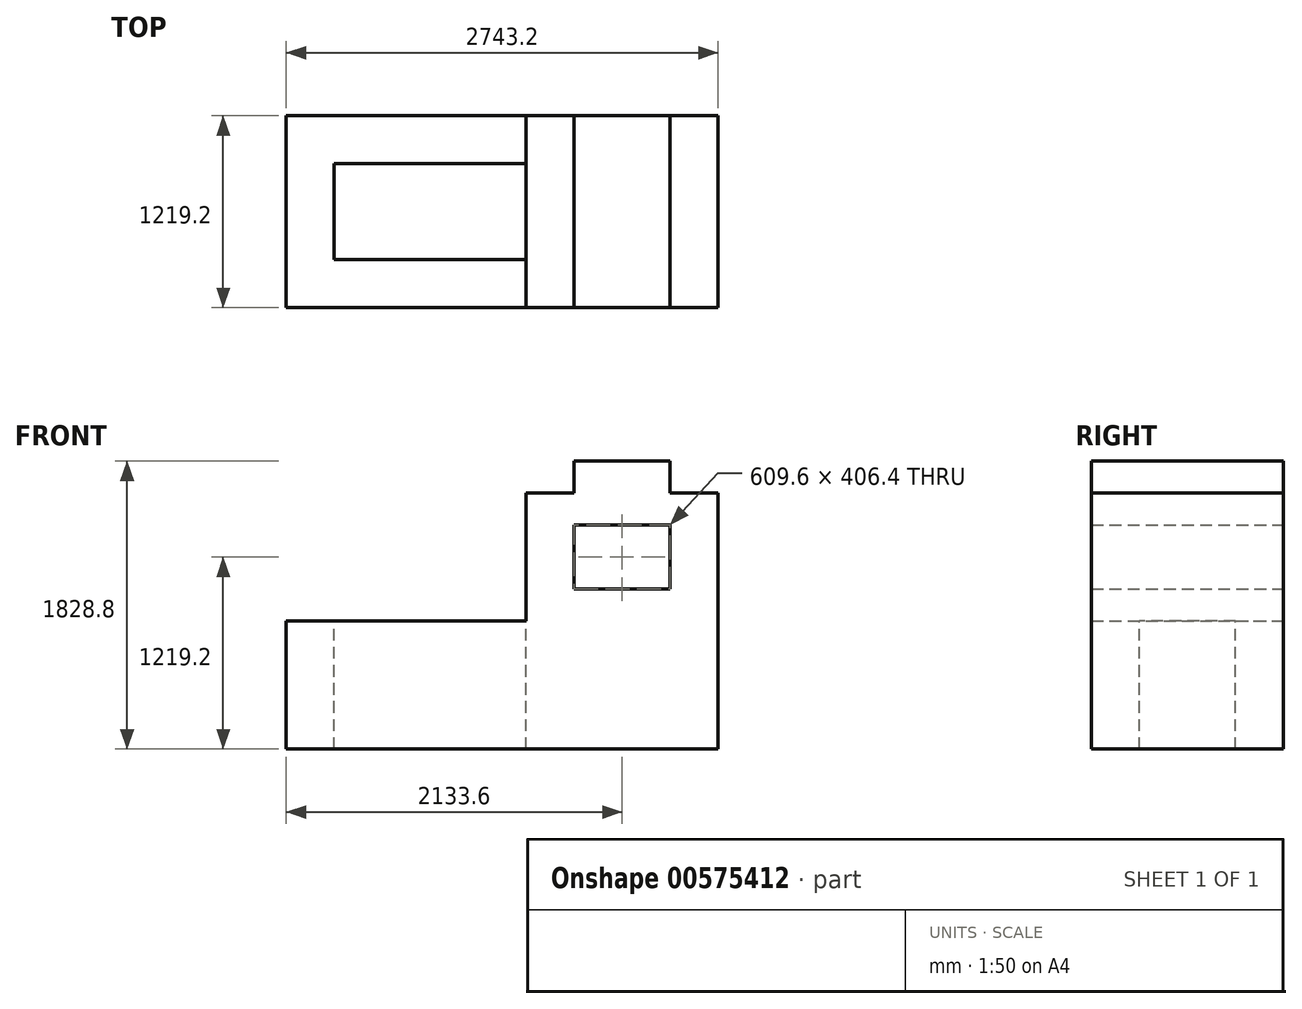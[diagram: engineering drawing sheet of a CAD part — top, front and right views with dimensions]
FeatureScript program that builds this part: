
annotation { "Feature Type Name" : "Feature", "Feature Type Description" : "" }
export const myFeature = defineFeature(function(context is Context, id is Id, definition is map)
    precondition{}
    {
        {
            var Q0;
            Q0=qCreatedBy(makeId("Front.planeOp"),FACE);
            var sketch = newSketch(context, id + "F0", { "sketchPlane" : qUnion([Q0])});
            skLineSegment(sketch, "E0", {"start": v(0, 0) * mm, "end": v(2743.2, 0) * mm});
            skLineSegment(sketch, "E1", {"start": v(2743.2, 0) * mm, "end": v(2743.2, 1625.6) * mm});
            skLineSegment(sketch, "E2", {"start": v(2743.2, 1625.6) * mm, "end": v(2438.4, 1625.6) * mm});
            skLineSegment(sketch, "E3", {"start": v(2438.4, 1625.6) * mm, "end": v(2438.4, 1828.8) * mm});
            skLineSegment(sketch, "E4", {"start": v(2438.4, 1828.8) * mm, "end": v(1828.8, 1828.8) * mm});
            skLineSegment(sketch, "E5", {"start": v(1828.8, 1828.8) * mm, "end": v(1828.8, 1625.6) * mm});
            skLineSegment(sketch, "E6", {"start": v(1828.8, 1625.6) * mm, "end": v(1524, 1625.6) * mm});
            skLineSegment(sketch, "E7", {"start": v(1524, 1625.6) * mm, "end": v(1524, 812.8) * mm});
            skLineSegment(sketch, "E8", {"start": v(1524, 812.8) * mm, "end": v(0, 812.8) * mm});
            skLineSegment(sketch, "E9", {"start": v(0, 812.8) * mm, "end": v(0, 0) * mm});
            skLineSegment(sketch, "E10", {"start": v(2438.4, 1422.4) * mm, "end": v(1828.8, 1422.4) * mm});
            skLineSegment(sketch, "E11", {"start": v(1828.8, 1422.4) * mm, "end": v(1828.8, 1016) * mm});
            skLineSegment(sketch, "E12", {"start": v(1828.8, 1016) * mm, "end": v(2438.4, 1016) * mm});
            skLineSegment(sketch, "E13", {"start": v(2438.4, 1016) * mm, "end": v(2438.4, 1422.4) * mm});
            skSolve(sketch);
        }
        {
            var Q0;
            Q0=makeQuery(id+"F0.imprint","IMPRINT",FACE,{"disambiguationData":[TD([[makeQuery(id+"F0.imprint","IMPRINT",EDGE,{"derivedFrom":sQuery(id+"F0.wireOp",EDGE,"E0")}),1.0]])]});
            extrude(context, id + "F1", {"entities" : qUnion([Q0]), "depth" : 1219.2 * mm, "offsetDistance" : 25.4 * mm});
        }
        {
            var Q0;
            Q0=makeQuery(id+"F1.opExtrude","SWEPT_FACE",FACE,{"disambiguationData":[OSD([sQuery(id+"F0.wireOp",EDGE,"E8")])]});
            var sketch = newSketch(context, id + "F2", { "sketchPlane" : qUnion([Q0])});
            skLineSegment(sketch, "E14", {"start": v(1524, 0) * mm, "end": v(1524, -304.8) * mm});
            skLineSegment(sketch, "E15", {"start": v(1524, -304.8) * mm, "end": v(304.8, -304.8) * mm});
            skLineSegment(sketch, "E16", {"start": v(304.8, -304.8) * mm, "end": v(304.8, -914.4) * mm});
            skLineSegment(sketch, "E17", {"start": v(304.8, -914.4) * mm, "end": v(1524, -914.4) * mm});
            skLineSegment(sketch, "E18", {"start": v(1524, -914.4) * mm, "end": v(1524, -304.8) * mm});
            skSolve(sketch);
        }
        {
            var Q0;
            Q0=makeQuery(id+"F2.imprint","IMPRINT",FACE,{"disambiguationData":[TD([[makeQuery(id+"F2.imprint","IMPRINT",EDGE,{"derivedFrom":sQuery(id+"F2.wireOp",EDGE,"E15")}),1.0]])]});
            extrude(context, id + "F3", {"entities" : qUnion([Q0]), "operationType" : NewBodyOperationType.REMOVE, "oppositeDirection" : true, "depth" : 812.8 * mm, "offsetDistance" : 25.4 * mm});
        }
    });
